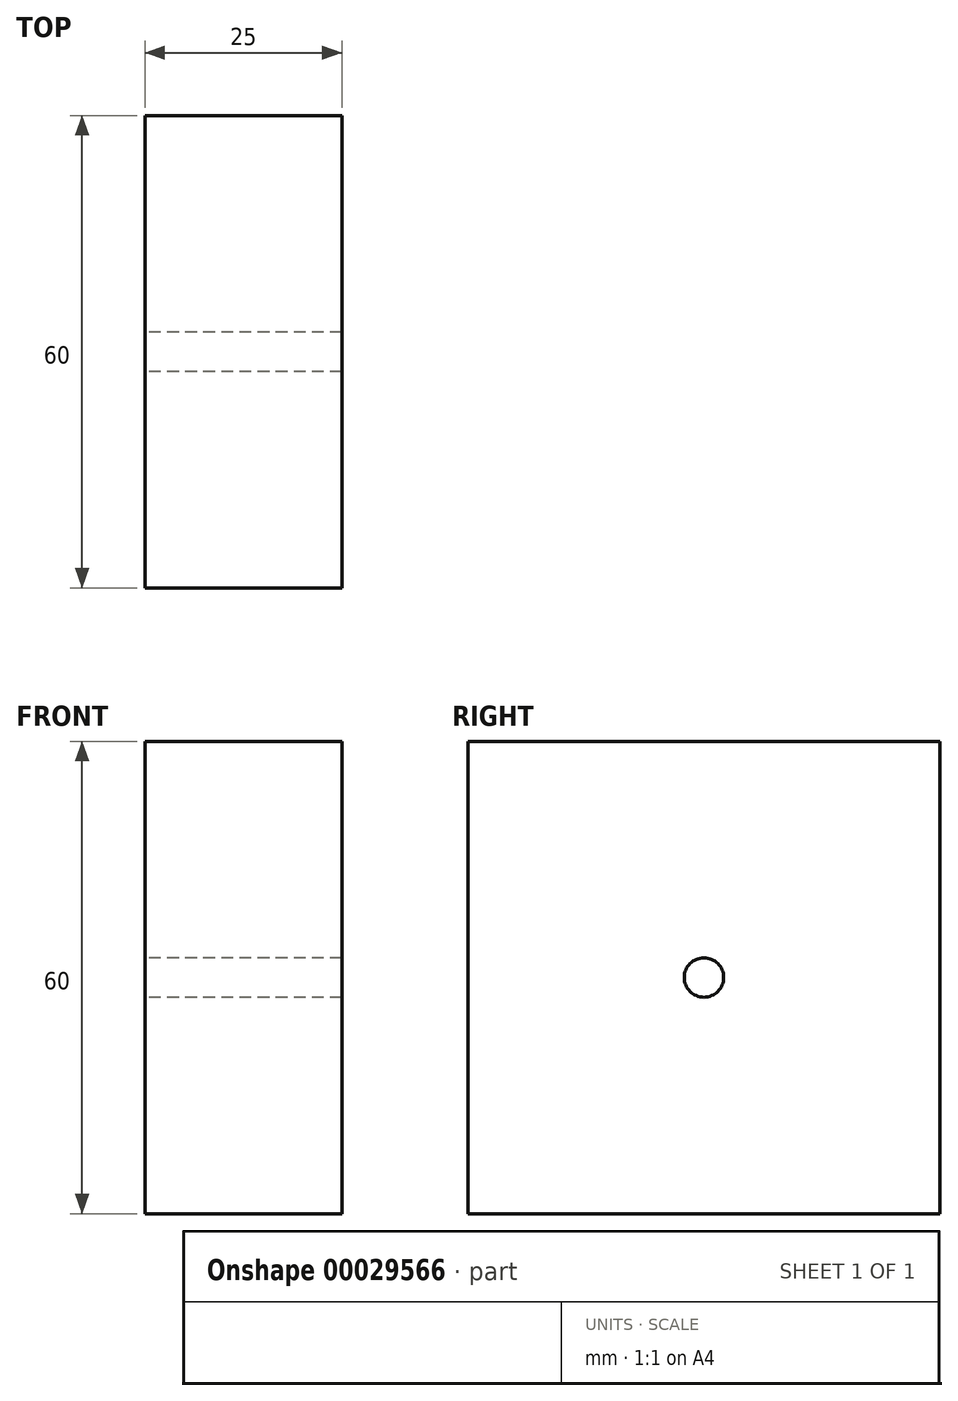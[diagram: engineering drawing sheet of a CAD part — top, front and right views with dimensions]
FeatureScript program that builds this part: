
annotation { "Feature Type Name" : "Feature", "Feature Type Description" : "" }
export const myFeature = defineFeature(function(context is Context, id is Id, definition is map)
    precondition{}
    {
        {
            var Q0;
            Q0=qCreatedBy(makeId("Right.planeOp"),FACE);
            var sketch = newSketch(context, id + "F0", { "sketchPlane" : qUnion([Q0])});
            skLineSegment(sketch, "E0.bottom", {"start": v(-30, 30) * mm, "end": v(30, 30) * mm});
            skLineSegment(sketch, "E0.top", {"start": v(-30, -30) * mm, "end": v(30, -30) * mm});
            skLineSegment(sketch, "E0.left", {"start": v(-30, 30) * mm, "end": v(-30, -30) * mm});
            skLineSegment(sketch, "E0.right", {"start": v(30, 30) * mm, "end": v(30, -30) * mm});
            skLineSegment(sketch, "E1", {"start": v(0, 0) * mm, "end": v(-30, 0) * mm});
            skLineSegment(sketch, "E2", {"start": v(0, 0) * mm, "end": v(30, 0) * mm});
            skLineSegment(sketch, "E3", {"start": v(0, -30) * mm, "end": v(0, 30) * mm});
            skCircle(sketch, "E4", {"center": v(0, 0) * mm, "radius": 12.5 * mm});
            skCircle(sketch, "E5", {"center": v(12.5, 0) * mm, "radius": 12.5 * mm});
            skCircle(sketch, "E6", {"center": v(-12.5, 0) * mm, "radius": 10 * mm});
            skSolve(sketch);
        }
        {
            var Q0;
            {var subQ7=sQuery(id+"F0.wireOp",EDGE,"E0.bottom");var subQ9=sQuery(id+"F0.wireOp",EDGE,"E0.right");var subQ11=makeQuery(id+"F0.imprint","INTERSECT",VERTEX,{"derivedFrom":[subQ7,subQ9]});Q0=makeQuery(id+"F0.imprint","IMPRINT",FACE,{"disambiguationData":[TD([[makeQuery(id+"F0.imprint","IMPRINT",EDGE,{"disambiguationData":[TD([[subQ11,1.0]])],"derivedFrom":subQ7}),-1.0]])]});}
            var Q1;
            {var subQ7=sQuery(id+"F0.wireOp",EDGE,"E0.bottom");var subQ9=sQuery(id+"F0.wireOp",EDGE,"E0.left");var subQ11=makeQuery(id+"F0.imprint","INTERSECT",VERTEX,{"derivedFrom":[subQ7,subQ9]});Q1=makeQuery(id+"F0.imprint","IMPRINT",FACE,{"disambiguationData":[TD([[makeQuery(id+"F0.imprint","IMPRINT",EDGE,{"disambiguationData":[TD([[subQ11,-1.0]])],"derivedFrom":subQ7}),-1.0]])]});}
            var Q2;
            {var subQ7=sQuery(id+"F0.wireOp",EDGE,"E0.top");var subQ9=sQuery(id+"F0.wireOp",EDGE,"E0.left");var subQ11=makeQuery(id+"F0.imprint","INTERSECT",VERTEX,{"derivedFrom":[subQ7,subQ9]});Q2=makeQuery(id+"F0.imprint","IMPRINT",FACE,{"disambiguationData":[TD([[makeQuery(id+"F0.imprint","IMPRINT",EDGE,{"disambiguationData":[TD([[subQ11,-1.0]])],"derivedFrom":subQ7}),1.0]])]});}
            var Q3;
            {var subQ7=sQuery(id+"F0.wireOp",EDGE,"E0.top");var subQ9=sQuery(id+"F0.wireOp",EDGE,"E0.right");var subQ11=makeQuery(id+"F0.imprint","INTERSECT",VERTEX,{"derivedFrom":[subQ7,subQ9]});Q3=makeQuery(id+"F0.imprint","IMPRINT",FACE,{"disambiguationData":[TD([[makeQuery(id+"F0.imprint","IMPRINT",EDGE,{"disambiguationData":[TD([[subQ11,1.0]])],"derivedFrom":subQ7}),1.0]])]});}
            var Q4;
            {var subQ1=sQuery(id+"F0.wireOp",EDGE,"E4");var subQ3=sQuery(id+"F0.wireOp",EDGE,"E2");var subQ5=makeQuery(id+"F0.imprint","INTERSECT",VERTEX,{"derivedFrom":[subQ3,subQ1]});Q4=makeQuery(id+"F0.imprint","IMPRINT",FACE,{"disambiguationData":[TD([[makeQuery(id+"F0.imprint","IMPRINT",EDGE,{"disambiguationData":[TD([[subQ5,-1.0]])],"derivedFrom":subQ3}),-1.0]])]});}
            var Q5;
            {var subQ1=sQuery(id+"F0.wireOp",EDGE,"E4");var subQ3=sQuery(id+"F0.wireOp",EDGE,"E2");var subQ5=makeQuery(id+"F0.imprint","INTERSECT",VERTEX,{"derivedFrom":[subQ3,subQ1]});Q5=makeQuery(id+"F0.imprint","IMPRINT",FACE,{"disambiguationData":[TD([[makeQuery(id+"F0.imprint","IMPRINT",EDGE,{"disambiguationData":[TD([[subQ5,-1.0]])],"derivedFrom":subQ3}),1.0]])]});}
            var Q6;
            {var subQ1=sQuery(id+"F0.wireOp",EDGE,"E4");var subQ3=sQuery(id+"F0.wireOp",EDGE,"E2");var subQ5=makeQuery(id+"F0.imprint","INTERSECT",VERTEX,{"derivedFrom":[subQ3,subQ1]});Q6=makeQuery(id+"F0.imprint","IMPRINT",FACE,{"disambiguationData":[TD([[makeQuery(id+"F0.imprint","IMPRINT",EDGE,{"disambiguationData":[TD([[subQ5,-1.0]])],"derivedFrom":subQ1}),1.0]])]});}
            var Q7;
            {var subQ1=sQuery(id+"F0.wireOp",EDGE,"E4");var subQ3=sQuery(id+"F0.wireOp",EDGE,"E2");var subQ5=makeQuery(id+"F0.imprint","INTERSECT",VERTEX,{"derivedFrom":[subQ3,subQ1]});Q7=makeQuery(id+"F0.imprint","IMPRINT",FACE,{"disambiguationData":[TD([[makeQuery(id+"F0.imprint","IMPRINT",EDGE,{"disambiguationData":[TD([[subQ5,1.0]])],"derivedFrom":subQ1}),1.0]])]});}
            var Q8;
            {var subQ1=sQuery(id+"F0.wireOp",EDGE,"E4");var subQ3=sQuery(id+"F0.wireOp",EDGE,"E3");var subQ5=makeQuery(id+"F0.imprint","INTERSECT",VERTEX,{"disambiguationData":[OD(0.0)],"derivedFrom":[subQ3,subQ1]});Q8=makeQuery(id+"F0.imprint","IMPRINT",FACE,{"disambiguationData":[TD([[makeQuery(id+"F0.imprint","IMPRINT",EDGE,{"disambiguationData":[TD([[subQ5,-1.0]])],"derivedFrom":subQ1}),1.0]])]});}
            var Q9;
            {var subQ1=sQuery(id+"F0.wireOp",EDGE,"E4");var subQ5=sQuery(id+"F0.wireOp",EDGE,"E3");var subQ6=makeQuery(id+"F0.imprint","INTERSECT",VERTEX,{"disambiguationData":[OD(0.0)],"derivedFrom":[subQ5,subQ1]});Q9=makeQuery(id+"F0.imprint","IMPRINT",FACE,{"disambiguationData":[TD([[makeQuery(id+"F0.imprint","IMPRINT",EDGE,{"disambiguationData":[TD([[subQ6,1.0]])],"derivedFrom":subQ1}),1.0]])]});}
            var Q10;
            {var subQ0=sQuery(id+"F0.wireOp",EDGE,"E6");var subQ3=sQuery(id+"F0.wireOp",EDGE,"E1");var subQ4=makeQuery(id+"F0.imprint","INTERSECT",VERTEX,{"disambiguationData":[OD(0.0)],"derivedFrom":[subQ3,subQ0]});Q10=makeQuery(id+"F0.imprint","IMPRINT",FACE,{"disambiguationData":[TD([[makeQuery(id+"F0.imprint","IMPRINT",EDGE,{"disambiguationData":[TD([[subQ4,-1.0]])],"derivedFrom":subQ3}),1.0]])]});}
            var Q11;
            {var subQ0=sQuery(id+"F0.wireOp",EDGE,"E6");var subQ3=sQuery(id+"F0.wireOp",EDGE,"E1");var subQ4=makeQuery(id+"F0.imprint","INTERSECT",VERTEX,{"disambiguationData":[OD(0.0)],"derivedFrom":[subQ3,subQ0]});Q11=makeQuery(id+"F0.imprint","IMPRINT",FACE,{"disambiguationData":[TD([[makeQuery(id+"F0.imprint","IMPRINT",EDGE,{"disambiguationData":[TD([[subQ4,-1.0]])],"derivedFrom":subQ3}),-1.0]])]});}
            var Q12;
            {var subQ1=sQuery(id+"F0.wireOp",EDGE,"E4");var subQ5=sQuery(id+"F0.wireOp",EDGE,"E3");var subQ6=makeQuery(id+"F0.imprint","INTERSECT",VERTEX,{"disambiguationData":[OD(1.0)],"derivedFrom":[subQ5,subQ1]});Q12=makeQuery(id+"F0.imprint","IMPRINT",FACE,{"disambiguationData":[TD([[makeQuery(id+"F0.imprint","IMPRINT",EDGE,{"disambiguationData":[TD([[subQ6,-1.0]])],"derivedFrom":subQ1}),1.0]])]});}
            var Q13;
            {var subQ1=sQuery(id+"F0.wireOp",EDGE,"E4");var subQ3=sQuery(id+"F0.wireOp",EDGE,"E3");var subQ5=makeQuery(id+"F0.imprint","INTERSECT",VERTEX,{"disambiguationData":[OD(1.0)],"derivedFrom":[subQ3,subQ1]});Q13=makeQuery(id+"F0.imprint","IMPRINT",FACE,{"disambiguationData":[TD([[makeQuery(id+"F0.imprint","IMPRINT",EDGE,{"disambiguationData":[TD([[subQ5,1.0]])],"derivedFrom":subQ1}),1.0]])]});}
            var Q14;
            {var subQ1=sQuery(id+"F0.wireOp",EDGE,"E4");var subQ3=sQuery(id+"F0.wireOp",EDGE,"E1");var subQ5=makeQuery(id+"F0.imprint","INTERSECT",VERTEX,{"derivedFrom":[subQ3,subQ1]});Q14=makeQuery(id+"F0.imprint","IMPRINT",FACE,{"disambiguationData":[TD([[makeQuery(id+"F0.imprint","IMPRINT",EDGE,{"disambiguationData":[TD([[subQ5,-1.0]])],"derivedFrom":subQ3}),-1.0]])]});}
            var Q15;
            {var subQ1=sQuery(id+"F0.wireOp",EDGE,"E4");var subQ3=sQuery(id+"F0.wireOp",EDGE,"E1");var subQ5=makeQuery(id+"F0.imprint","INTERSECT",VERTEX,{"derivedFrom":[subQ3,subQ1]});Q15=makeQuery(id+"F0.imprint","IMPRINT",FACE,{"disambiguationData":[TD([[makeQuery(id+"F0.imprint","IMPRINT",EDGE,{"disambiguationData":[TD([[subQ5,-1.0]])],"derivedFrom":subQ3}),1.0]])]});}
            extrude(context, id + "F1", {"entities" : qUnion([Q0, Q1, Q2, Q3, Q4, Q5, Q6, Q7, Q8, Q9, Q10, Q11, Q12, Q13, Q14, Q15]), "depth" : 25 * mm});
        }
        {
            var Q0;
            Q0=sQuery(id+"F0.wireOp",VERTEX,"E2.start");
            var Q1;
            Q1=makeQuery(id+"F1.opExtrude","SWEPT_BODY",BODY,{"disambiguationData":[OSD([sQuery(id+"F0.wireOp",EDGE,"E0.bottom"),sQuery(id+"F0.wireOp",EDGE,"E0.top"),sQuery(id+"F0.wireOp",EDGE,"E0.left"),sQuery(id+"F0.wireOp",EDGE,"E0.right")])]});
            hole(context, id + "F2", {"style" : HoleStyle.SIMPLE, "holeDiameter" : 5 * mm, "endStyle" : HoleEndStyle.THROUGH, "oppositeDirection" : true, "locations" : qUnion([Q0]), "scope" : qUnion([Q1])});
        }
    });
